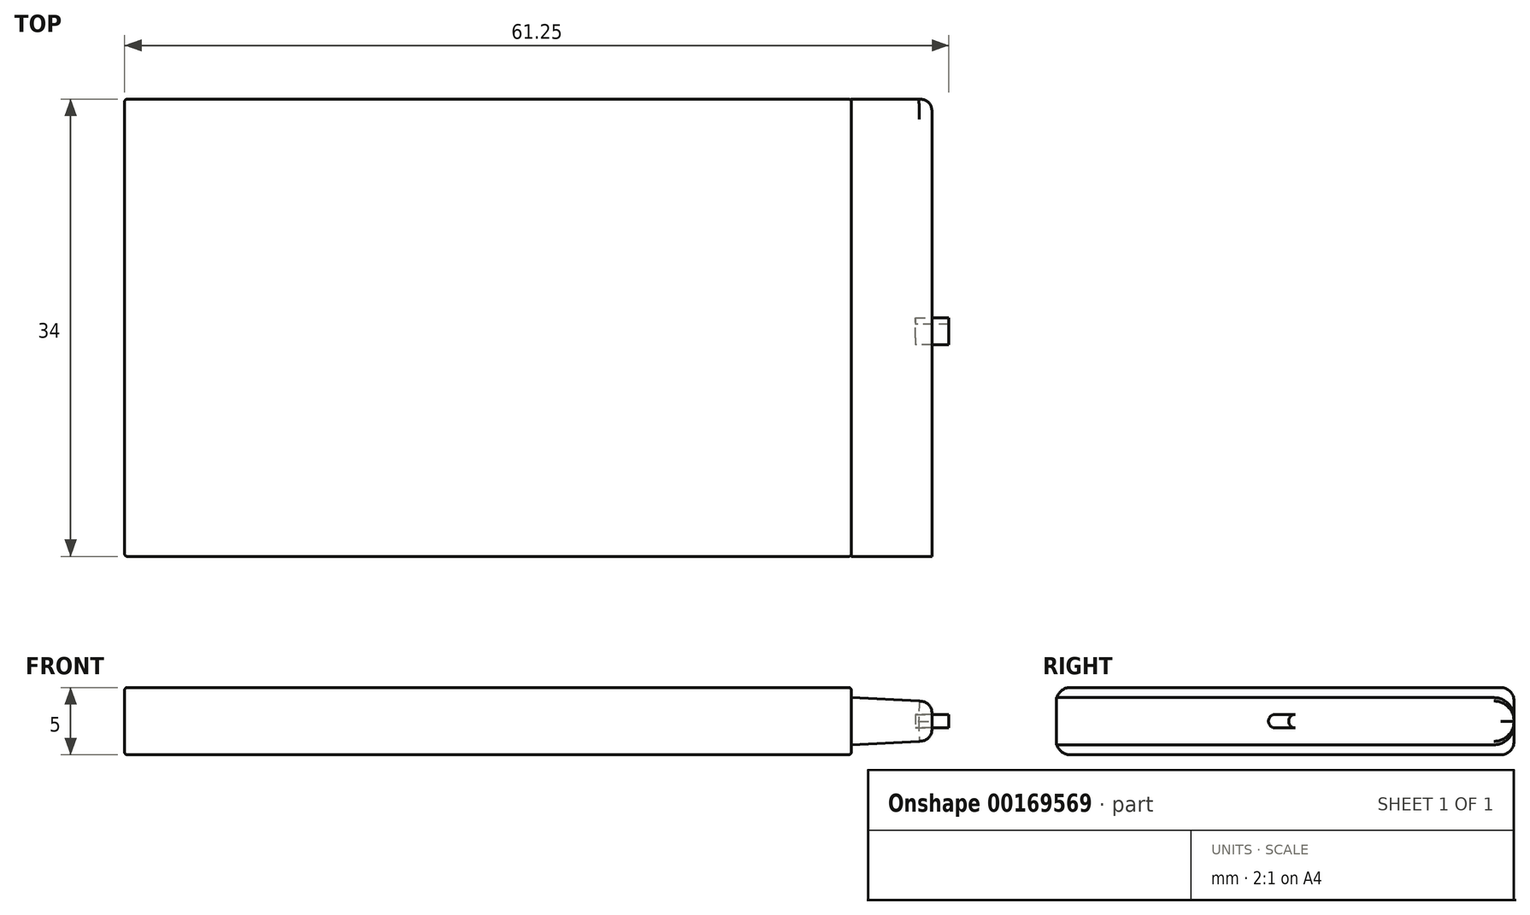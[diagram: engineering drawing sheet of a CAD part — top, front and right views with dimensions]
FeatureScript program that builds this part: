
annotation { "Feature Type Name" : "Feature", "Feature Type Description" : "" }
export const myFeature = defineFeature(function(context is Context, id is Id, definition is map)
    precondition{}
    {
        {
            var Q0;
            Q0=qCreatedBy(makeId("Top.planeOp"),FACE);
            var sketch = newSketch(context, id + "F0", { "sketchPlane" : qUnion([Q0])});
            skLineSegment(sketch, "E0.bottom", {"start": v(27, 17) * mm, "end": v(-27, 17) * mm});
            skLineSegment(sketch, "E0.top", {"start": v(27, -17) * mm, "end": v(-27, -17) * mm});
            skLineSegment(sketch, "E0.left", {"start": v(27, 17) * mm, "end": v(27, -17) * mm});
            skLineSegment(sketch, "E0.right", {"start": v(-27, 17) * mm, "end": v(-27, -17) * mm});
            skPoint(sketch, "E0.middle", {"position": v(0, 0) * mm});
            skSolve(sketch);
        }
        {
            var Q0;
            Q0=makeQuery(id+"F0.imprint","IMPRINT",FACE,{"disambiguationData":[TD([[makeQuery(id+"F0.imprint","IMPRINT",EDGE,{"derivedFrom":sQuery(id+"F0.wireOp",EDGE,"E0.bottom")}),1.0]])]});
            extrude(context, id + "F1", {"entities" : qUnion([Q0]), "depth" : 5 * mm});
        }
        {
            var Q0;
            Q0=makeQuery(id+"F1.opExtrude","SWEPT_FACE",FACE,{"disambiguationData":[OSD([sQuery(id+"F0.wireOp",EDGE,"E0.left")])]});
            var sketch = newSketch(context, id + "F2", { "sketchPlane" : qUnion([Q0])});
            skLineSegment(sketch, "E1", {"start": v(-17, 2.5) * mm, "end": v(17, 2.5) * mm, "construction": true});
            skLineSegment(sketch, "E2.bottom", {"start": v(-17, 4.25) * mm, "end": v(17, 4.25) * mm});
            skLineSegment(sketch, "E2.top", {"start": v(-17, 0.75) * mm, "end": v(17, 0.75) * mm});
            skLineSegment(sketch, "E2.left", {"start": v(-17, 4.25) * mm, "end": v(-17, 0.75) * mm});
            skLineSegment(sketch, "E2.right", {"start": v(17, 4.25) * mm, "end": v(17, 0.75) * mm});
            skSolve(sketch);
        }
        {
            var Q0;
            Q0=makeQuery(id+"F2.imprint","IMPRINT",FACE,{"disambiguationData":[TD([[makeQuery(id+"F2.imprint","IMPRINT",EDGE,{"derivedFrom":sQuery(id+"F2.wireOp",EDGE,"E2.bottom")}),-1.0]])]});
            extrude(context, id + "F3", {"entities" : qUnion([Q0]), "depth" : 6 * mm});
        }
        {
            var Q0;
            Q0=makeQuery(id+"F3.opExtrude","SWEPT_FACE",FACE,{"disambiguationData":[OSD([sQuery(id+"F2.wireOp",EDGE,"E2.left")])]});
            var sketch = newSketch(context, id + "F4", { "sketchPlane" : qUnion([Q0])});
            skLineSegment(sketch, "E3", {"start": v(27, 4.25) * mm, "end": v(33, 3.95) * mm});
            skLineSegment(sketch, "E4", {"start": v(33, 3.95) * mm, "end": v(33, 4.25) * mm});
            skLineSegment(sketch, "E5", {"start": v(33, 4.25) * mm, "end": v(27, 4.25) * mm});
            skLineSegment(sketch, "E6", {"start": v(27, 0.75) * mm, "end": v(33, 0.75) * mm});
            skLineSegment(sketch, "E7", {"start": v(33, 0.75) * mm, "end": v(33, 1.05) * mm});
            skLineSegment(sketch, "E8", {"start": v(33, 1.05) * mm, "end": v(27, 0.75) * mm});
            skSolve(sketch);
        }
        {
            var Q0;
            Q0=makeQuery(id+"F4.imprint","IMPRINT",FACE,{"disambiguationData":[TD([[makeQuery(id+"F4.imprint","IMPRINT",EDGE,{"derivedFrom":sQuery(id+"F4.wireOp",EDGE,"E3")}),1.0]])]});
            var Q1;
            Q1=makeQuery(id+"F4.imprint","IMPRINT",FACE,{"disambiguationData":[TD([[makeQuery(id+"F4.imprint","IMPRINT",EDGE,{"derivedFrom":sQuery(id+"F4.wireOp",EDGE,"E6")}),-1.0]])]});
            extrude(context, id + "F5", {"entities" : qUnion([Q0, Q1]), "operationType" : NewBodyOperationType.REMOVE, "endBound" : BoundingType.THROUGH_ALL, "oppositeDirection" : true, "depth" : 25 * mm});
        }
        {
            var Q0;
            Q0=makeQuery(id+"F1.opExtrude","CAP_EDGE",EDGE,{"disambiguationData":[OSD([sQuery(id+"F0.wireOp",EDGE,"E0.top")])],"isStart":false});
            var Q1;
            Q1=makeQuery(id+"F1.opExtrude","CAP_EDGE",EDGE,{"disambiguationData":[OSD([sQuery(id+"F0.wireOp",EDGE,"E0.top")])],"isStart":true});
            var Q2;
            Q2=makeQuery(id+"F1.opExtrude","CAP_EDGE",EDGE,{"disambiguationData":[OSD([sQuery(id+"F0.wireOp",EDGE,"E0.bottom")])],"isStart":false});
            var Q3;
            Q3=makeQuery(id+"F1.opExtrude","CAP_EDGE",EDGE,{"disambiguationData":[OSD([sQuery(id+"F0.wireOp",EDGE,"E0.bottom")])],"isStart":true});
            fillet(context, id + "F6", {"entities" : qUnion([Q0, Q1, Q2, Q3]), "radius" : 1 * mm, "tangentPropagation" : true, "allowEdgeOverflow" : false});
        }
        {
            var Q0;
            Q0=makeQuery(id+"F1.opExtrude","CAP_EDGE",EDGE,{"disambiguationData":[OSD([sQuery(id+"F0.wireOp",EDGE,"E0.right")])],"isStart":false});
            var Q1;
            Q1=makeQuery(id+"F1.opExtrude","SWEPT_FACE",FACE,{"disambiguationData":[OSD([sQuery(id+"F0.wireOp",EDGE,"E0.right")])]});
            var Q2;
            Q2=makeQuery(id+"F1.opExtrude","CAP_EDGE",EDGE,{"disambiguationData":[OSD([sQuery(id+"F0.wireOp",EDGE,"E0.right")])],"isStart":true});
            var Q3;
            Q3=makeQuery(id+"F6.opFillet","BLEND_EDGE",EDGE,{"blendedFrom":[makeQuery(id+"F1.opExtrude","CAP_EDGE",EDGE,{"disambiguationData":[OSD([sQuery(id+"F0.wireOp",EDGE,"E0.bottom")])],"isStart":false}),makeQuery(id+"F1.opExtrude","SWEPT_FACE",FACE,{"disambiguationData":[OSD([sQuery(id+"F0.wireOp",EDGE,"E0.right")])]})],"blendedInto":[makeQuery(id+"F1.opExtrude","SWEPT_FACE",FACE,{"disambiguationData":[OSD([sQuery(id+"F0.wireOp",EDGE,"E0.right")])]})]});
            var Q4;
            Q4=makeQuery(id+"F1.opExtrude","SWEPT_EDGE",EDGE,{"disambiguationData":[OSD([sQuery(id+"F0.wireOp",EDGE,"E0.bottom"),sQuery(id+"F0.wireOp",EDGE,"E0.right")])]});
            var Q5;
            Q5=makeQuery(id+"F6.opFillet","BLEND_EDGE",EDGE,{"blendedFrom":[makeQuery(id+"F1.opExtrude","CAP_EDGE",EDGE,{"disambiguationData":[OSD([sQuery(id+"F0.wireOp",EDGE,"E0.bottom")])],"isStart":true}),makeQuery(id+"F1.opExtrude","SWEPT_FACE",FACE,{"disambiguationData":[OSD([sQuery(id+"F0.wireOp",EDGE,"E0.right")])]})],"blendedInto":[makeQuery(id+"F1.opExtrude","SWEPT_FACE",FACE,{"disambiguationData":[OSD([sQuery(id+"F0.wireOp",EDGE,"E0.right")])]})]});
            var Q6;
            Q6=makeQuery(id+"F6.opFillet","BLEND_EDGE",EDGE,{"blendedFrom":[makeQuery(id+"F1.opExtrude","CAP_EDGE",EDGE,{"disambiguationData":[OSD([sQuery(id+"F0.wireOp",EDGE,"E0.top")])],"isStart":false}),makeQuery(id+"F1.opExtrude","SWEPT_FACE",FACE,{"disambiguationData":[OSD([sQuery(id+"F0.wireOp",EDGE,"E0.right")])]})],"blendedInto":[makeQuery(id+"F1.opExtrude","SWEPT_FACE",FACE,{"disambiguationData":[OSD([sQuery(id+"F0.wireOp",EDGE,"E0.right")])]})]});
            var Q7;
            Q7=makeQuery(id+"F1.opExtrude","SWEPT_EDGE",EDGE,{"disambiguationData":[OSD([sQuery(id+"F0.wireOp",EDGE,"E0.top"),sQuery(id+"F0.wireOp",EDGE,"E0.right")])]});
            var Q8;
            Q8=makeQuery(id+"F6.opFillet","BLEND_EDGE",EDGE,{"blendedFrom":[makeQuery(id+"F1.opExtrude","CAP_EDGE",EDGE,{"disambiguationData":[OSD([sQuery(id+"F0.wireOp",EDGE,"E0.top")])],"isStart":true}),makeQuery(id+"F1.opExtrude","SWEPT_FACE",FACE,{"disambiguationData":[OSD([sQuery(id+"F0.wireOp",EDGE,"E0.right")])]})],"blendedInto":[makeQuery(id+"F1.opExtrude","SWEPT_FACE",FACE,{"disambiguationData":[OSD([sQuery(id+"F0.wireOp",EDGE,"E0.right")])]})]});
            fillet(context, id + "F7", {"entities" : qUnion([Q0, Q1, Q2, Q3, Q4, Q5, Q6, Q7, Q8]), "radius" : 0.2 * mm, "tangentPropagation" : true, "allowEdgeOverflow" : false});
        }
        {
            var Q0;
            Q0=makeQuery(id+"F6.opFillet","BLEND_EDGE",EDGE,{"blendedFrom":[makeQuery(id+"F1.opExtrude","CAP_EDGE",EDGE,{"disambiguationData":[OSD([sQuery(id+"F0.wireOp",EDGE,"E0.top")])],"isStart":false}),makeQuery(id+"F1.opExtrude","SWEPT_FACE",FACE,{"disambiguationData":[OSD([sQuery(id+"F0.wireOp",EDGE,"E0.left")])]})],"blendedInto":[makeQuery(id+"F1.opExtrude","SWEPT_FACE",FACE,{"disambiguationData":[OSD([sQuery(id+"F0.wireOp",EDGE,"E0.left")])]})]});
            var Q1;
            Q1=makeQuery(id+"F1.opExtrude","CAP_EDGE",EDGE,{"disambiguationData":[OSD([sQuery(id+"F0.wireOp",EDGE,"E0.left")])],"isStart":false});
            var Q2;
            Q2=makeQuery(id+"F6.opFillet","BLEND_EDGE",EDGE,{"blendedFrom":[makeQuery(id+"F1.opExtrude","CAP_EDGE",EDGE,{"disambiguationData":[OSD([sQuery(id+"F0.wireOp",EDGE,"E0.bottom")])],"isStart":false}),makeQuery(id+"F1.opExtrude","SWEPT_FACE",FACE,{"disambiguationData":[OSD([sQuery(id+"F0.wireOp",EDGE,"E0.left")])]})],"blendedInto":[makeQuery(id+"F1.opExtrude","SWEPT_FACE",FACE,{"disambiguationData":[OSD([sQuery(id+"F0.wireOp",EDGE,"E0.left")])]})]});
            var Q3;
            Q3=makeQuery(id+"F6.opFillet","BLEND_EDGE",EDGE,{"blendedFrom":[makeQuery(id+"F1.opExtrude","CAP_EDGE",EDGE,{"disambiguationData":[OSD([sQuery(id+"F0.wireOp",EDGE,"E0.bottom")])],"isStart":true}),makeQuery(id+"F1.opExtrude","SWEPT_FACE",FACE,{"disambiguationData":[OSD([sQuery(id+"F0.wireOp",EDGE,"E0.left")])]})],"blendedInto":[makeQuery(id+"F1.opExtrude","SWEPT_FACE",FACE,{"disambiguationData":[OSD([sQuery(id+"F0.wireOp",EDGE,"E0.left")])]})]});
            var Q4;
            Q4=makeQuery(id+"F1.opExtrude","CAP_EDGE",EDGE,{"disambiguationData":[OSD([sQuery(id+"F0.wireOp",EDGE,"E0.left")])],"isStart":true});
            var Q5;
            Q5=makeQuery(id+"F6.opFillet","BLEND_EDGE",EDGE,{"blendedFrom":[makeQuery(id+"F1.opExtrude","CAP_EDGE",EDGE,{"disambiguationData":[OSD([sQuery(id+"F0.wireOp",EDGE,"E0.top")])],"isStart":true}),makeQuery(id+"F1.opExtrude","SWEPT_FACE",FACE,{"disambiguationData":[OSD([sQuery(id+"F0.wireOp",EDGE,"E0.left")])]})],"blendedInto":[makeQuery(id+"F1.opExtrude","SWEPT_FACE",FACE,{"disambiguationData":[OSD([sQuery(id+"F0.wireOp",EDGE,"E0.left")])]})]});
            fillet(context, id + "F8", {"entities" : qUnion([Q0, Q1, Q2, Q3, Q4, Q5]), "radius" : 0.2 * mm, "tangentPropagation" : true, "allowEdgeOverflow" : false});
        }
        {
            var Q0;
            Q0=makeQuery(id+"F5.boolean.opBoolean","COPY",EDGE,{"derivedFrom":makeQuery(id+"F5.opExtrude","CAP_EDGE",EDGE,{"disambiguationData":[OSD([sQuery(id+"F4.wireOp",EDGE,"E3")])],"isStart":true})});
            var Q1;
            Q1=makeQuery(id+"F5.boolean.opBoolean","COPY",EDGE,{"derivedFrom":makeQuery(id+"F5.opExtrude","CAP_EDGE",EDGE,{"disambiguationData":[OSD([sQuery(id+"F4.wireOp",EDGE,"E8")])],"isStart":true})});
            var Q2;
            Q2=makeQuery(id+"F5.boolean.opBoolean","INTERSECT",EDGE,{"derivedFrom":[makeQuery(id+"F3.opExtrude","SWEPT_FACE",FACE,{"disambiguationData":[OSD([sQuery(id+"F2.wireOp",EDGE,"E2.right")])]}),makeQuery(id+"F5.opExtrude","SWEPT_FACE",FACE,{"disambiguationData":[OSD([sQuery(id+"F4.wireOp",EDGE,"E3")])]})]});
            var Q3;
            Q3=makeQuery(id+"F5.boolean.opBoolean","INTERSECT",EDGE,{"derivedFrom":[makeQuery(id+"F3.opExtrude","SWEPT_FACE",FACE,{"disambiguationData":[OSD([sQuery(id+"F2.wireOp",EDGE,"E2.right")])]}),makeQuery(id+"F5.opExtrude","SWEPT_FACE",FACE,{"disambiguationData":[OSD([sQuery(id+"F4.wireOp",EDGE,"E8")])]})]});
            fillet(context, id + "F9", {"entities" : qUnion([Q0, Q1, Q2, Q3]), "radius" : 1.5 * mm, "allowEdgeOverflow" : false});
        }
        {
            var Q0;
            Q0=makeQuery(id+"F9.opFillet","BLEND_EDGE",EDGE,{"blendedFrom":[makeQuery(id+"F5.boolean.opBoolean","COPY",EDGE,{"derivedFrom":makeQuery(id+"F5.opExtrude","CAP_EDGE",EDGE,{"disambiguationData":[OSD([sQuery(id+"F4.wireOp",EDGE,"E3")])],"isStart":true})}),makeQuery(id+"F3.opExtrude","CAP_FACE",FACE,{"disambiguationData":[OSD([sQuery(id+"F2.wireOp",EDGE,"E2.bottom"),sQuery(id+"F2.wireOp",EDGE,"E2.top"),sQuery(id+"F2.wireOp",EDGE,"E2.left"),sQuery(id+"F2.wireOp",EDGE,"E2.right")])],"isStart":false})],"blendedInto":[makeQuery(id+"F3.opExtrude","CAP_FACE",FACE,{"disambiguationData":[OSD([sQuery(id+"F2.wireOp",EDGE,"E2.bottom"),sQuery(id+"F2.wireOp",EDGE,"E2.top"),sQuery(id+"F2.wireOp",EDGE,"E2.left"),sQuery(id+"F2.wireOp",EDGE,"E2.right")])],"isStart":false})]});
            var Q1;
            Q1=makeQuery(id+"F9.opFillet","BLEND_EDGE",EDGE,{"blendedFrom":[makeQuery(id+"F5.boolean.opBoolean","COPY",EDGE,{"derivedFrom":makeQuery(id+"F5.opExtrude","CAP_EDGE",EDGE,{"disambiguationData":[OSD([sQuery(id+"F4.wireOp",EDGE,"E8")])],"isStart":true})}),makeQuery(id+"F3.opExtrude","CAP_FACE",FACE,{"disambiguationData":[OSD([sQuery(id+"F2.wireOp",EDGE,"E2.bottom"),sQuery(id+"F2.wireOp",EDGE,"E2.top"),sQuery(id+"F2.wireOp",EDGE,"E2.left"),sQuery(id+"F2.wireOp",EDGE,"E2.right")])],"isStart":false})],"blendedInto":[makeQuery(id+"F3.opExtrude","CAP_FACE",FACE,{"disambiguationData":[OSD([sQuery(id+"F2.wireOp",EDGE,"E2.bottom"),sQuery(id+"F2.wireOp",EDGE,"E2.top"),sQuery(id+"F2.wireOp",EDGE,"E2.left"),sQuery(id+"F2.wireOp",EDGE,"E2.right")])],"isStart":false})]});
            var Q2;
            Q2=makeQuery(id+"F5.boolean.opBoolean","COPY",EDGE,{"derivedFrom":makeQuery(id+"F5.opExtrude","SWEPT_EDGE",EDGE,{"disambiguationData":[OSD([sQuery(id+"F2.wireOp",EDGE,"E2.left"),sQuery(id+"F4.wireOp",EDGE,"E7"),sQuery(id+"F4.wireOp",EDGE,"E8")])]})});
            var Q3;
            {var subQ0=sQuery(id+"F2.wireOp",EDGE,"E2.right");Q3=makeQuery(id+"F9.opFillet","BLEND_EDGE",EDGE,{"blendedFrom":[makeQuery(id+"F5.boolean.opBoolean","INTERSECT",EDGE,{"derivedFrom":[makeQuery(id+"F3.opExtrude","SWEPT_FACE",FACE,{"disambiguationData":[OSD([subQ0])]}),makeQuery(id+"F5.opExtrude","SWEPT_FACE",FACE,{"disambiguationData":[OSD([sQuery(id+"F4.wireOp",EDGE,"E8")])]})]}),makeQuery(id+"F3.opExtrude","CAP_FACE",FACE,{"disambiguationData":[OSD([sQuery(id+"F2.wireOp",EDGE,"E2.bottom"),sQuery(id+"F2.wireOp",EDGE,"E2.top"),sQuery(id+"F2.wireOp",EDGE,"E2.left"),subQ0])],"isStart":false})],"blendedInto":[makeQuery(id+"F3.opExtrude","CAP_FACE",FACE,{"disambiguationData":[OSD([sQuery(id+"F2.wireOp",EDGE,"E2.bottom"),sQuery(id+"F2.wireOp",EDGE,"E2.top"),sQuery(id+"F2.wireOp",EDGE,"E2.left"),subQ0])],"isStart":false})]});}
            var Q4;
            {var subQ0=sQuery(id+"F2.wireOp",EDGE,"E2.right");Q4=makeQuery(id+"F9.opFillet","BLEND_EDGE",EDGE,{"blendedFrom":[makeQuery(id+"F5.boolean.opBoolean","INTERSECT",EDGE,{"derivedFrom":[makeQuery(id+"F3.opExtrude","SWEPT_FACE",FACE,{"disambiguationData":[OSD([subQ0])]}),makeQuery(id+"F5.opExtrude","SWEPT_FACE",FACE,{"disambiguationData":[OSD([sQuery(id+"F4.wireOp",EDGE,"E3")])]})]}),makeQuery(id+"F3.opExtrude","CAP_FACE",FACE,{"disambiguationData":[OSD([sQuery(id+"F2.wireOp",EDGE,"E2.bottom"),sQuery(id+"F2.wireOp",EDGE,"E2.top"),sQuery(id+"F2.wireOp",EDGE,"E2.left"),subQ0])],"isStart":false})],"blendedInto":[makeQuery(id+"F3.opExtrude","CAP_FACE",FACE,{"disambiguationData":[OSD([sQuery(id+"F2.wireOp",EDGE,"E2.bottom"),sQuery(id+"F2.wireOp",EDGE,"E2.top"),sQuery(id+"F2.wireOp",EDGE,"E2.left"),subQ0])],"isStart":false})]});}
            var Q5;
            Q5=makeQuery(id+"F5.boolean.opBoolean","COPY",EDGE,{"derivedFrom":makeQuery(id+"F5.opExtrude","SWEPT_EDGE",EDGE,{"disambiguationData":[OSD([sQuery(id+"F2.wireOp",EDGE,"E2.left"),sQuery(id+"F4.wireOp",EDGE,"E3"),sQuery(id+"F4.wireOp",EDGE,"E4")])]})});
            fillet(context, id + "F10", {"entities" : qUnion([Q0, Q1, Q2, Q3, Q4, Q5]), "radius" : 1 * mm, "tangentPropagation" : true, "rho" : 0.5, "crossSection" : FilletCrossSection.CONIC, "allowEdgeOverflow" : false});
        }
        {
            var Q0;
            Q0=makeQuery(id+"F3.opExtrude","CAP_FACE",FACE,{"disambiguationData":[OSD([sQuery(id+"F2.wireOp",EDGE,"E2.bottom"),sQuery(id+"F2.wireOp",EDGE,"E2.top"),sQuery(id+"F2.wireOp",EDGE,"E2.left"),sQuery(id+"F2.wireOp",EDGE,"E2.right")])],"isStart":false});
            var sketch = newSketch(context, id + "F11", { "sketchPlane" : qUnion([Q0])});
            skLineSegment(sketch, "E9", {"start": v(-16, 2.5) * mm, "end": v(16, 2.5) * mm, "construction": true});
            skLineSegment(sketch, "E10", {"start": v(0, 3) * mm, "end": v(0, 2) * mm, "construction": true});
            skCircle(sketch, "E11", {"center": v(-0.75, 2.5) * mm, "radius": 0.5 * mm});
            skCircle(sketch, "E12.MirrorC", {"center": v(0.75, 2.5) * mm, "radius": 0.5 * mm});
            skSolve(sketch);
        }
        {
            var Q0;
            {var subQ0=sQuery(id+"F11.wireOp",EDGE,"E11");var subQ1=sQuery(id+"F2.wireOp",EDGE,"E2.left");var subQ2=makeQuery(id+"F3.opExtrude","CAP_FACE",FACE,{"disambiguationData":[OSD([sQuery(id+"F2.wireOp",EDGE,"E2.bottom"),sQuery(id+"F2.wireOp",EDGE,"E2.top"),subQ1,sQuery(id+"F2.wireOp",EDGE,"E2.right")])],"isStart":false});var subQ3=makeQuery(id+"F11.imprint","INTERSECT",VERTEX,{"derivedFrom":[makeQuery(id+"F10.opFillet","BLEND_EDGE",EDGE,{"blendedFrom":[makeQuery(id+"F5.boolean.opBoolean","COPY",EDGE,{"derivedFrom":makeQuery(id+"F5.opExtrude","SWEPT_EDGE",EDGE,{"disambiguationData":[OSD([subQ1,sQuery(id+"F4.wireOp",EDGE,"E3"),sQuery(id+"F4.wireOp",EDGE,"E4")])]})}),subQ2],"blendedInto":[subQ2]}),subQ0]});Q0=makeQuery(id+"F11.imprint","IMPRINT",FACE,{"disambiguationData":[TD([[makeQuery(id+"F11.imprint","IMPRINT",EDGE,{"disambiguationData":[TD([[subQ3,-1.0]])],"derivedFrom":subQ0}),1.0]])]});}
            var Q1;
            {var subQ0=sQuery(id+"F11.wireOp",EDGE,"E12.MirrorC");var subQ1=sQuery(id+"F2.wireOp",EDGE,"E2.left");var subQ2=makeQuery(id+"F3.opExtrude","CAP_FACE",FACE,{"disambiguationData":[OSD([sQuery(id+"F2.wireOp",EDGE,"E2.bottom"),sQuery(id+"F2.wireOp",EDGE,"E2.top"),subQ1,sQuery(id+"F2.wireOp",EDGE,"E2.right")])],"isStart":false});var subQ3=makeQuery(id+"F11.imprint","INTERSECT",VERTEX,{"derivedFrom":[makeQuery(id+"F10.opFillet","BLEND_EDGE",EDGE,{"blendedFrom":[makeQuery(id+"F5.boolean.opBoolean","COPY",EDGE,{"derivedFrom":makeQuery(id+"F5.opExtrude","SWEPT_EDGE",EDGE,{"disambiguationData":[OSD([subQ1,sQuery(id+"F4.wireOp",EDGE,"E3"),sQuery(id+"F4.wireOp",EDGE,"E4")])]})}),subQ2],"blendedInto":[subQ2]}),subQ0]});Q1=makeQuery(id+"F11.imprint","IMPRINT",FACE,{"disambiguationData":[TD([[makeQuery(id+"F11.imprint","IMPRINT",EDGE,{"disambiguationData":[TD([[subQ3,-1.0]])],"derivedFrom":subQ0}),-1.0]])]});}
            extrude(context, id + "F12", {"entities" : qUnion([Q0, Q1]), "depth" : 2.5 * mm, "symmetric" : true});
        }
    });
